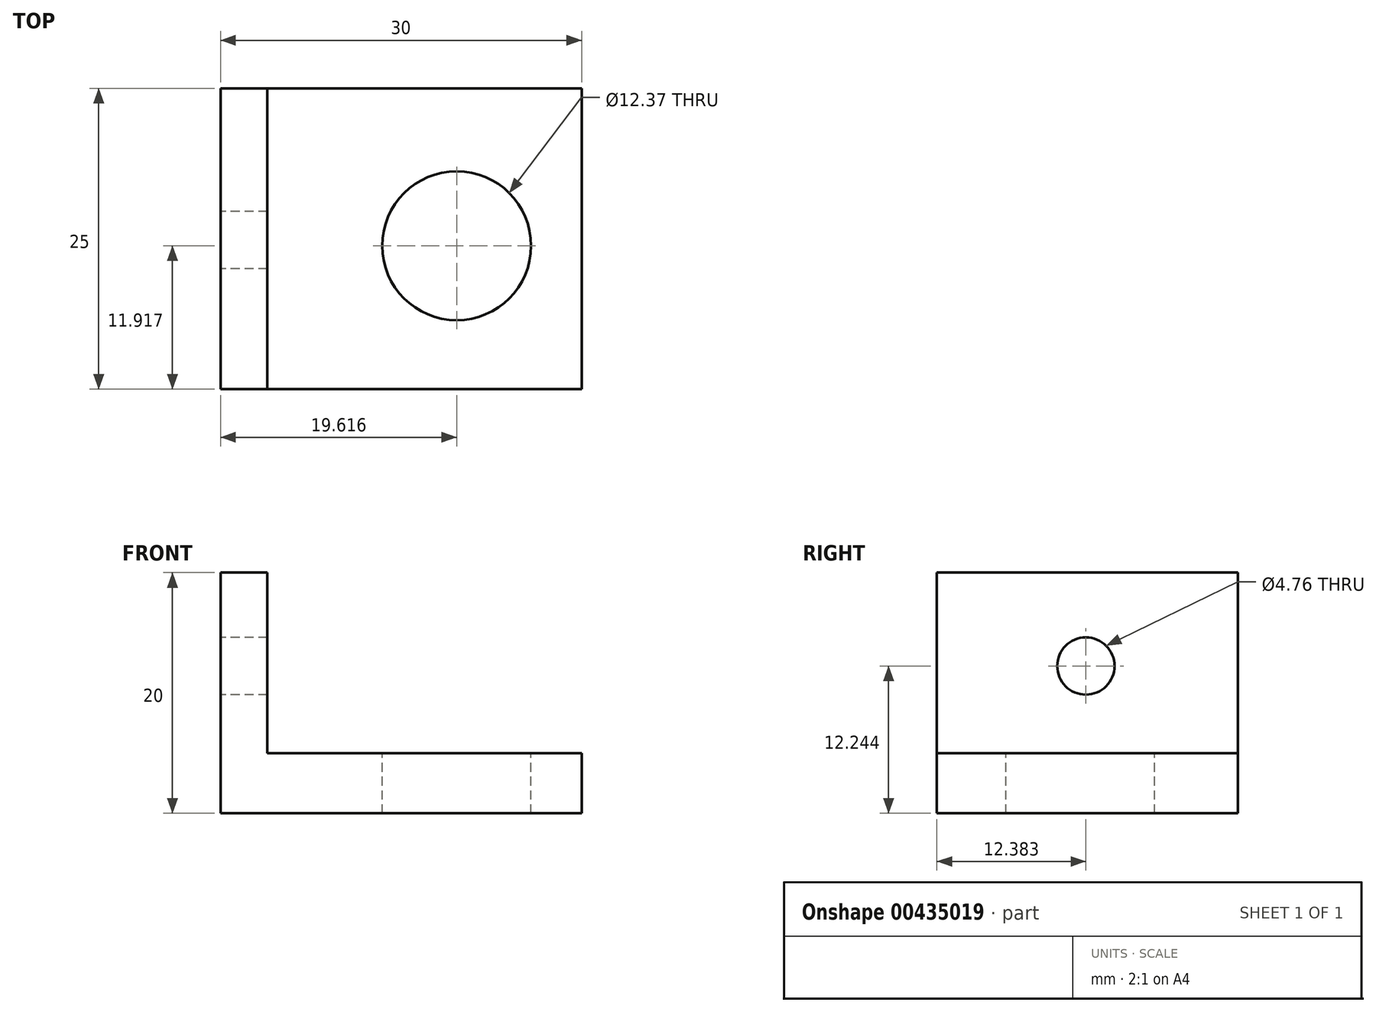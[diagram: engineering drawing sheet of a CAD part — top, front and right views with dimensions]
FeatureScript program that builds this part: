
annotation { "Feature Type Name" : "Feature", "Feature Type Description" : "" }
export const myFeature = defineFeature(function(context is Context, id is Id, definition is map)
    precondition{}
    {
        {
            var Q0;
            Q0=qCreatedBy(makeId("Top.planeOp"),FACE);
            var sketch = newSketch(context, id + "F0", { "sketchPlane" : qUnion([Q0])});
            skLineSegment(sketch, "E0.bottom", {"start": v(-13.48, 17.43) * mm, "end": v(16.52, 17.43) * mm});
            skLineSegment(sketch, "E0.top", {"start": v(-13.48, -7.57) * mm, "end": v(16.52, -7.57) * mm});
            skLineSegment(sketch, "E0.left", {"start": v(-13.48, 17.43) * mm, "end": v(-13.48, -7.57) * mm});
            skLineSegment(sketch, "E0.right", {"start": v(16.52, 17.43) * mm, "end": v(16.52, -7.57) * mm});
            skLineSegment(sketch, "E1", {"start": v(-9.6, 17.43) * mm, "end": v(-9.6, -7.57) * mm});
            skSolve(sketch);
        }
        {
            var Q0;
            {var subQ0=sQuery(id+"F0.wireOp",EDGE,"E0.left");Q0=makeQuery(id+"F0.imprint","IMPRINT",FACE,{"disambiguationData":[TD([[makeQuery(id+"F0.imprint","IMPRINT",EDGE,{"derivedFrom":subQ0}),1.0]])]});}
            var sketch = newSketch(context, id + "F1", { "sketchPlane" : qUnion([Q0])});
            skSolve(sketch);
        }
        {
            var Q0;
            {var subQ0=sQuery(id+"F0.wireOp",EDGE,"E0.left");Q0=makeQuery(id+"F0.imprint","IMPRINT",FACE,{"disambiguationData":[TD([[makeQuery(id+"F0.imprint","IMPRINT",EDGE,{"derivedFrom":subQ0}),1.0]])]});}
            extrude(context, id + "F2", {"entities" : qUnion([Q0]), "depth" : 20 * mm});
        }
        {
            var Q0;
            Q0 = qSketchRegion(id + "F1", true);
            var Q1;
            Q1 = qSketchRegion(id + "F0", true);
            extrude(context, id + "F3", {"entities" : qUnion([Q0, Q1]), "operationType" : NewBodyOperationType.ADD, "depth" : 5 * mm});
        }
        {
            var Q0;
            Q0=makeQuery(id+"F2.opExtrude","SWEPT_FACE",FACE,{"disambiguationData":[OSD([sQuery(id+"F0.wireOp",EDGE,"E0.left")])]});
            var sketch = newSketch(context, id + "F4", { "sketchPlane" : qUnion([Q0])});
            skCircle(sketch, "E2", {"center": v(-4.81, 12.24) * mm, "radius": 2.38 * mm});
            skSolve(sketch);
        }
        {
            var Q0;
            Q0 = qSketchRegion(id + "F4", true);
            extrude(context, id + "F5", {"entities" : qUnion([Q0]), "operationType" : NewBodyOperationType.REMOVE, "oppositeDirection" : true, "depth" : 25 * mm});
        }
        {
            var Q0;
            Q0=makeQuery(id+"F3.opExtrude","CAP_FACE",FACE,{"disambiguationData":[OSD([sQuery(id+"F0.wireOp",EDGE,"E0.bottom"),sQuery(id+"F0.wireOp",EDGE,"E0.top"),sQuery(id+"F0.wireOp",EDGE,"E0.left"),sQuery(id+"F0.wireOp",EDGE,"E0.right")])],"isStart":false});
            var sketch = newSketch(context, id + "F6", { "sketchPlane" : qUnion([Q0])});
            skCircle(sketch, "E3", {"center": v(6.14, 4.35) * mm, "radius": 6.18 * mm});
            skSolve(sketch);
        }
        {
            var Q0;
            Q0 = qSketchRegion(id + "F6", true);
            extrude(context, id + "F7", {"entities" : qUnion([Q0]), "operationType" : NewBodyOperationType.REMOVE, "oppositeDirection" : true, "depth" : 6 * mm});
        }
    });
